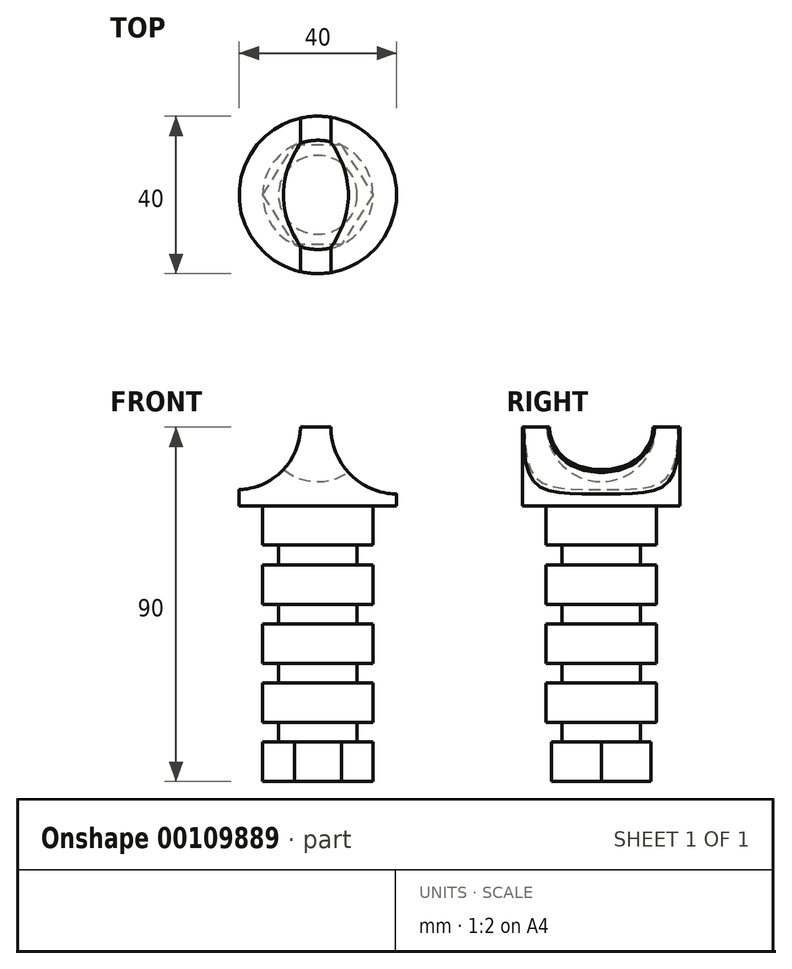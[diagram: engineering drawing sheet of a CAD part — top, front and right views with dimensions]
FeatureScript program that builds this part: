
annotation { "Feature Type Name" : "Feature", "Feature Type Description" : "" }
export const myFeature = defineFeature(function(context is Context, id is Id, definition is map)
    precondition{}
    {
        {
            var Q0;
            Q0=qCreatedBy(makeId("Top.planeOp"),FACE);
            var sketch = newSketch(context, id + "F0", { "sketchPlane" : qUnion([Q0])});
            skCircle(sketch, "E0", {"center": v(0, 0) * mm, "radius": 10 * mm});
            skSolve(sketch);
        }
        {
            var Q0;
            Q0=makeQuery(id+"F0.imprint","IMPRINT",FACE,{"disambiguationData":[TD([[makeQuery(id+"F0.imprint","IMPRINT",EDGE,{"derivedFrom":sQuery(id+"F0.wireOp",EDGE,"E0")}),1.0]])]});
            extrude(context, id + "F1", {"entities" : qUnion([Q0]), "depth" : 80 * mm});
        }
        {
            var Q0;
            Q0=qCreatedBy(makeId("Top.planeOp"),FACE);
            var sketch = newSketch(context, id + "F2", { "sketchPlane" : qUnion([Q0])});
            skLineSegment(sketch, "E1.bottom", {"start": v(5.97, 12.66) * mm, "end": v(-5.97, 12.66) * mm});
            skLineSegment(sketch, "E1.top", {"start": v(5.97, -12.66) * mm, "end": v(-5.97, -12.66) * mm});
            skPoint(sketch, "E1.middle", {"position": v(0, 0) * mm});
            skLineSegment(sketch, "E2", {"start": v(-14, 0) * mm, "end": v(-5.97, -12.66) * mm});
            skLineSegment(sketch, "E3", {"start": v(-14, 0) * mm, "end": v(-5.97, 12.66) * mm});
            skLineSegment(sketch, "E4", {"start": v(-5.97, 12.66) * mm, "end": v(-0.03, 12.66) * mm});
            skLineSegment(sketch, "E5", {"start": v(-5.97, -12.66) * mm, "end": v(0.03, -12.66) * mm});
            skLineSegment(sketch, "E6", {"start": v(-0.03, 12.66) * mm, "end": v(5.97, 12.66) * mm});
            skLineSegment(sketch, "E7", {"start": v(5.97, 12.66) * mm, "end": v(14, 0) * mm});
            skLineSegment(sketch, "E8", {"start": v(14, 0) * mm, "end": v(5.97, -12.66) * mm});
            skLineSegment(sketch, "E9", {"start": v(5.97, -12.66) * mm, "end": v(0.03, -12.66) * mm});
            skPoint(sketch, "E10.orphan", {"position": v(14.03, -12.66) * mm});
            skPoint(sketch, "E11.orphan", {"position": v(13.97, 12.66) * mm});
            skPoint(sketch, "E12.orphan", {"position": v(-14.03, 12.66) * mm});
            skPoint(sketch, "E13.orphan", {"position": v(-13.97, -12.66) * mm});
            skSolve(sketch);
        }
        {
            var Q0;
            Q0=makeQuery(id+"F2.imprint","IMPRINT",FACE,{"disambiguationData":[TD([[makeQuery(id+"F2.imprint","IMPRINT",EDGE,{"derivedFrom":sQuery(id+"F2.wireOp",EDGE,"E2")}),1.0]])]});
            extrude(context, id + "F3", {"entities" : qUnion([Q0]), "operationType" : NewBodyOperationType.ADD, "depth" : 10 * mm});
        }
        {
            var Q0;
            Q0=makeQuery(id+"F3.opExtrude","CAP_FACE",FACE,{"disambiguationData":[OSD([sQuery(id+"F2.wireOp",EDGE,"E2"),sQuery(id+"F2.wireOp",EDGE,"E3"),sQuery(id+"F2.wireOp",EDGE,"E4"),sQuery(id+"F2.wireOp",EDGE,"E5"),sQuery(id+"F2.wireOp",EDGE,"E6"),sQuery(id+"F2.wireOp",EDGE,"E7"),sQuery(id+"F2.wireOp",EDGE,"E8"),sQuery(id+"F2.wireOp",EDGE,"E9")])],"isStart":false});
            var sketch = newSketch(context, id + "F4", { "sketchPlane" : qUnion([Q0])});
            skSolve(sketch);
        }
        {
            var Q0;
            {var subQ5=sQuery(id+"F2.wireOp",EDGE,"E2");Q0=makeQuery(id+"F4.imprint","IMPRINT",FACE,{"disambiguationData":[TD([[makeQuery(id+"F4.imprint","IMPRINT",EDGE,{"derivedFrom":makeQuery(id+"F3.opExtrude","CAP_EDGE",EDGE,{"disambiguationData":[OSD([subQ5])],"isStart":false})}),1.0]])]});}
            cPlane(context, id + "F5", {"entities" : qUnion([Q0]), "cplaneType" : CPlaneType.OFFSET, "offset" : 5 * mm, "width" : 150 * mm, "height" : 150 * mm});
        }
        {
            var Q0;
            Q0=qCreatedBy(id+"F5.planeOp",FACE);
            var sketch = newSketch(context, id + "F6", { "sketchPlane" : qUnion([Q0])});
            skCircle(sketch, "E14", {"center": v(0, 0) * mm, "radius": 14 * mm});
            skSolve(sketch);
        }
        {
            var Q0;
            Q0=makeQuery(id+"F6.imprint","IMPRINT",FACE,{"disambiguationData":[TD([[makeQuery(id+"F6.imprint","IMPRINT",EDGE,{"derivedFrom":sQuery(id+"F6.wireOp",EDGE,"E14")}),1.0]])]});
            extrude(context, id + "F7", {"entities" : qUnion([Q0]), "operationType" : NewBodyOperationType.ADD, "depth" : 10 * mm});
        }
        {
            var Q0;
            Q0=makeQuery(id+"F7.opExtrude","CAP_FACE",FACE,{"disambiguationData":[OSD([sQuery(id+"F6.wireOp",EDGE,"E14")])],"isStart":false});
            cPlane(context, id + "F8", {"entities" : qUnion([Q0]), "cplaneType" : CPlaneType.OFFSET, "offset" : 5 * mm, "width" : 150 * mm, "height" : 150 * mm});
        }
        {
            var Q0;
            Q0=qCreatedBy(id+"F8.planeOp",FACE);
            var sketch = newSketch(context, id + "F9", { "sketchPlane" : qUnion([Q0])});
            skCircle(sketch, "E15", {"center": v(0, 0) * mm, "radius": 14 * mm});
            skSolve(sketch);
        }
        {
            var Q0;
            Q0=makeQuery(id+"F9.imprint","IMPRINT",FACE,{"disambiguationData":[TD([[makeQuery(id+"F9.imprint","IMPRINT",EDGE,{"derivedFrom":sQuery(id+"F9.wireOp",EDGE,"E15")}),1.0]])]});
            extrude(context, id + "F10", {"entities" : qUnion([Q0]), "operationType" : NewBodyOperationType.ADD, "depth" : 10 * mm});
        }
        {
            var Q0;
            Q0=makeQuery(id+"F10.opExtrude","CAP_FACE",FACE,{"disambiguationData":[OSD([sQuery(id+"F9.wireOp",EDGE,"E15")])],"isStart":false});
            cPlane(context, id + "F11", {"entities" : qUnion([Q0]), "cplaneType" : CPlaneType.OFFSET, "offset" : 5 * mm, "width" : 150 * mm, "height" : 150 * mm});
        }
        {
            var Q0;
            Q0=qCreatedBy(id+"F11.planeOp",FACE);
            var sketch = newSketch(context, id + "F12", { "sketchPlane" : qUnion([Q0])});
            skCircle(sketch, "E16", {"center": v(0, 0) * mm, "radius": 14 * mm});
            skSolve(sketch);
        }
        {
            var Q0;
            Q0 = qSketchRegion(id + "F12", true);
            extrude(context, id + "F13", {"entities" : qUnion([Q0]), "operationType" : NewBodyOperationType.ADD, "depth" : 10 * mm});
        }
        {
            var Q0;
            Q0=makeQuery(id+"F13.opExtrude","CAP_FACE",FACE,{"disambiguationData":[OSD([sQuery(id+"F12.wireOp",EDGE,"E16")])],"isStart":false});
            cPlane(context, id + "F14", {"entities" : qUnion([Q0]), "cplaneType" : CPlaneType.OFFSET, "offset" : 5 * mm, "width" : 150 * mm, "height" : 150 * mm});
        }
        {
            var Q0;
            Q0=qCreatedBy(id+"F14.planeOp",FACE);
            var sketch = newSketch(context, id + "F15", { "sketchPlane" : qUnion([Q0])});
            skCircle(sketch, "E17", {"center": v(0, 0) * mm, "radius": 14 * mm});
            skSolve(sketch);
        }
        {
            var Q0;
            Q0=makeQuery(id+"F15.imprint","IMPRINT",FACE,{"disambiguationData":[TD([[makeQuery(id+"F15.imprint","IMPRINT",EDGE,{"derivedFrom":sQuery(id+"F15.wireOp",EDGE,"E17")}),1.0]])]});
            extrude(context, id + "F16", {"entities" : qUnion([Q0]), "operationType" : NewBodyOperationType.ADD, "depth" : 10 * mm});
        }
        {
            var Q0;
            Q0=makeQuery(id+"F16.opExtrude","CAP_FACE",FACE,{"disambiguationData":[OSD([sQuery(id+"F15.wireOp",EDGE,"E17")])],"isStart":false});
            var sketch = newSketch(context, id + "F17", { "sketchPlane" : qUnion([Q0])});
            skCircle(sketch, "E18", {"center": v(0, 0) * mm, "radius": 20 * mm});
            skSolve(sketch);
        }
        {
            var Q0;
            Q0 = qSketchRegion(id + "F17", true);
            extrude(context, id + "F18", {"entities" : qUnion([Q0]), "operationType" : NewBodyOperationType.ADD, "depth" : 20 * mm});
        }
        {
            var Q0;
            Q0=makeQuery(id+"F18.opExtrude","CAP_FACE",FACE,{"disambiguationData":[OSD([sQuery(id+"F17.wireOp",EDGE,"E18")])],"isStart":false});
            var sketch = newSketch(context, id + "F19", { "sketchPlane" : qUnion([Q0])});
            skArc(sketch, "E19", {"start": v(0, 13.87) * mm, "mid": v(-13.87, 0) * mm, "end": v(0, -13.87) * mm});
            skLineSegment(sketch, "E20", {"start": v(0, 13.87) * mm, "end": v(0, -13.87) * mm});
            skSolve(sketch);
        }
        {
            var Q0;
            Q0=makeQuery(id+"F19.imprint","IMPRINT",FACE,{"disambiguationData":[TD([[makeQuery(id+"F19.imprint","IMPRINT",EDGE,{"derivedFrom":sQuery(id+"F19.wireOp",EDGE,"E19")}),1.0]])]});
            var Q1;
            Q1=sQuery(id+"F19.wireOp",EDGE,"E20");
            revolve(context, id + "F20", {"operationType" : NewBodyOperationType.REMOVE, "entities" : qUnion([Q0]), "axis" : qUnion([Q1]), "revolveType" : RevolveType.FULL});
        }
        {
            var Q0;
            Q0=qCreatedBy(makeId("Front.planeOp"),FACE);
            var sketch = newSketch(context, id + "F21", { "sketchPlane" : qUnion([Q0])});
            skArc(sketch, "E21", {"start": v(20.3, 107) * mm, "mid": v(3.29, 90) * mm, "end": v(20.3, 73) * mm});
            skLineSegment(sketch, "E22", {"start": v(20.3, 90) * mm, "end": v(20.3, 107) * mm});
            skLineSegment(sketch, "E23", {"start": v(20.3, 107) * mm, "end": v(20.3, 73) * mm});
            skSolve(sketch);
        }
        {
            var Q0;
            Q0 = qSketchRegion(id + "F21", true);
            var Q1;
            {var subQ0=sQuery(id+"F21.wireOp",EDGE,"E21");Q1=makeQuery(id+"F21.imprint","IMPRINT",FACE,{"disambiguationData":[TD([[makeQuery(id+"F21.imprint","IMPRINT",EDGE,{"derivedFrom":subQ0}),1.0]])]});}
            extrude(context, id + "F22", {"entities" : qUnion([Q0, Q1]), "operationType" : NewBodyOperationType.REMOVE, "depth" : 25 * mm, "hasSecondDirection" : true, "secondDirectionOppositeDirection" : true, "secondDirectionDepth" : 25 * mm});
        }
        {
            var Q0;
            Q0=qCreatedBy(makeId("Front.planeOp"),FACE);
            var sketch = newSketch(context, id + "F23", { "sketchPlane" : qUnion([Q0])});
            skCircle(sketch, "E24", {"center": v(-20.43, 90.13) * mm, "radius": 16 * mm});
            skSolve(sketch);
        }
        {
            var Q0;
            Q0=makeQuery(id+"F23.imprint","IMPRINT",FACE,{"disambiguationData":[TD([[makeQuery(id+"F23.imprint","IMPRINT",EDGE,{"derivedFrom":sQuery(id+"F23.wireOp",EDGE,"E24")}),1.0]])]});
            extrude(context, id + "F24", {"entities" : qUnion([Q0]), "operationType" : NewBodyOperationType.REMOVE, "oppositeDirection" : true, "depth" : 25 * mm, "hasSecondDirection" : true, "secondDirectionOppositeDirection" : false, "secondDirectionDepth" : 25 * mm});
        }
    });
